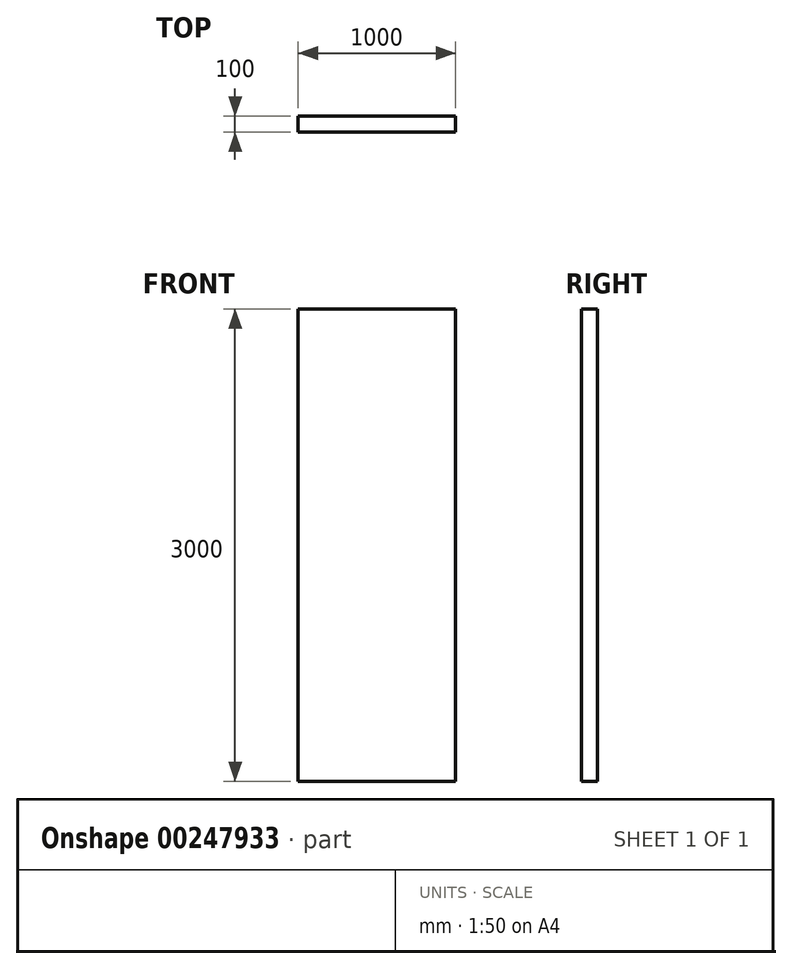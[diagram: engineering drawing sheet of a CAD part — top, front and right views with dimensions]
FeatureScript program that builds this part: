
annotation { "Feature Type Name" : "Feature", "Feature Type Description" : "" }
export const myFeature = defineFeature(function(context is Context, id is Id, definition is map)
    precondition{}
    {
        {
            var Q0;
            Q0=qCreatedBy(makeId("Front.planeOp"),FACE);
            var sketch = newSketch(context, id + "F0", { "sketchPlane" : qUnion([Q0])});
            skLineSegment(sketch, "E0.bottom", {"start": v(500, 0) * mm, "end": v(-500, 0) * mm});
            skLineSegment(sketch, "E0.top", {"start": v(500, 3000) * mm, "end": v(-500, 3000) * mm});
            skLineSegment(sketch, "E0.left", {"start": v(500, 0) * mm, "end": v(500, 3000) * mm});
            skLineSegment(sketch, "E0.right", {"start": v(-500, 0) * mm, "end": v(-500, 3000) * mm});
            skPoint(sketch, "E0.middle", {"position": v(0, 1500) * mm});
            skSolve(sketch);
        }
        {
            var Q0;
            Q0=makeQuery(id+"F0.imprint","IMPRINT",FACE,{"disambiguationData":[TD([[makeQuery(id+"F0.imprint","IMPRINT",EDGE,{"derivedFrom":sQuery(id+"F0.wireOp",EDGE,"E0.bottom")}),-1.0]])]});
            extrude(context, id + "F1", {"entities" : qUnion([Q0]), "endBound" : BoundingType.SYMMETRIC, "depth" : 100 * mm});
        }
    });
